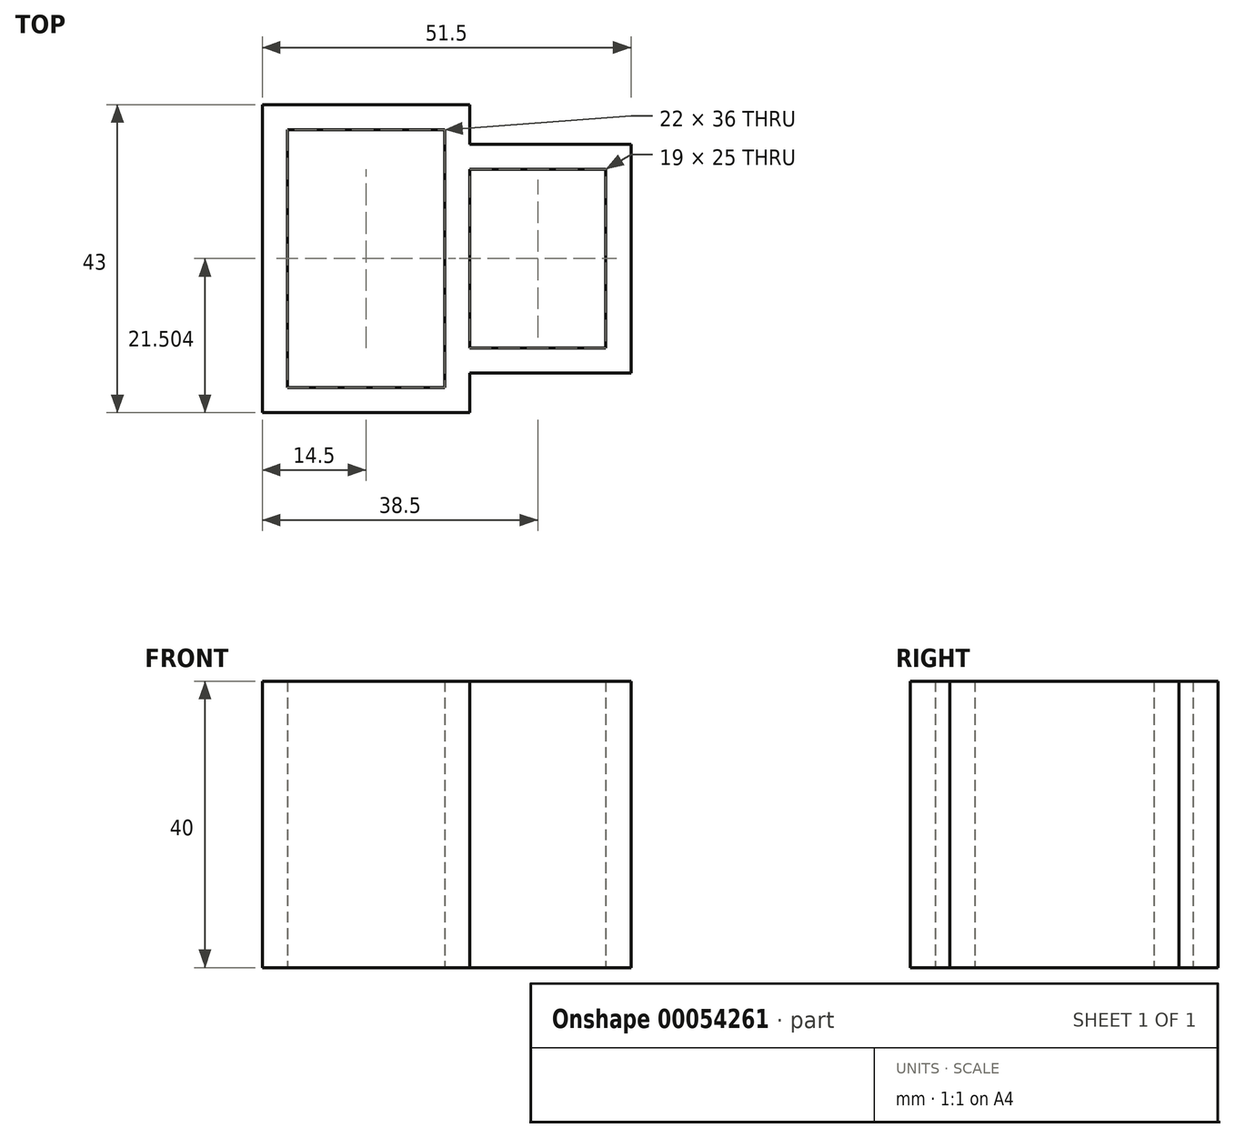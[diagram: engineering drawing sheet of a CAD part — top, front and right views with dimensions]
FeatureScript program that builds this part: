
annotation { "Feature Type Name" : "Feature", "Feature Type Description" : "" }
export const myFeature = defineFeature(function(context is Context, id is Id, definition is map)
    precondition{}
    {
        {
            var Q0;
            Q0=qCreatedBy(makeId("Top.planeOp"),FACE);
            var sketch = newSketch(context, id + "F0", { "sketchPlane" : qUnion([Q0])});
            skLineSegment(sketch, "E0.bottom", {"start": v(0, -10.9) * mm, "end": v(19, -10.9) * mm});
            skLineSegment(sketch, "E0.top", {"start": v(0, 14.1) * mm, "end": v(19, 14.1) * mm});
            skLineSegment(sketch, "E0.left", {"start": v(0, -10.9) * mm, "end": v(0, 14.1) * mm});
            skLineSegment(sketch, "E0.right", {"start": v(19, -10.9) * mm, "end": v(19, 14.1) * mm});
            skLineSegment(sketch, "E1.0", {"start": v(0, 17.6) * mm, "end": v(22.5, 17.6) * mm});
            skLineSegment(sketch, "E1.1", {"start": v(-3.5, -14.4) * mm, "end": v(-3.5, 17.6) * mm});
            skLineSegment(sketch, "E1.2", {"start": v(0, -14.4) * mm, "end": v(22.5, -14.4) * mm});
            skLineSegment(sketch, "E1.3", {"start": v(22.5, -14.4) * mm, "end": v(22.5, 17.6) * mm});
            skLineSegment(sketch, "E2.0", {"start": v(-25.5, -8.02) * mm, "end": v(-25.5, 11.23) * mm});
            skPoint(sketch, "E3", {"position": v(-25.5, 1.6) * mm});
            skLineSegment(sketch, "E4.0", {"start": v(-29, -8.02) * mm, "end": v(-29, 23.98) * mm});
            skLineSegment(sketch, "E5", {"start": v(-25.5, 1.6) * mm, "end": v(22.5, 1.6) * mm, "construction": true});
            skLineSegment(sketch, "E6.0", {"start": v(-25.5, -16.4) * mm, "end": v(-3.5, -16.4) * mm});
            skLineSegment(sketch, "E7.MirrorCS", {"start": v(-25.5, 19.6) * mm, "end": v(-3.5, 19.6) * mm});
            skLineSegment(sketch, "E8", {"start": v(-3.5, 17.6) * mm, "end": v(-3.5, 19.6) * mm});
            skLineSegment(sketch, "E9", {"start": v(-3.5, 19.6) * mm, "end": v(-3.5, -14.4) * mm});
            skLineSegment(sketch, "E10", {"start": v(-3.5, -14.4) * mm, "end": v(-3.5, -16.4) * mm});
            skLineSegment(sketch, "E11", {"start": v(-25.5, 19.6) * mm, "end": v(-25.5, 11.23) * mm});
            skLineSegment(sketch, "E12", {"start": v(-25.5, -8.02) * mm, "end": v(-25.5, -16.4) * mm});
            skPoint(sketch, "E13.orphan", {"position": v(22.5, 19.6) * mm});
            skPoint(sketch, "E14.orphan", {"position": v(22.5, -16.4) * mm});
            skLineSegment(sketch, "E15", {"start": v(-29, 23.98) * mm, "end": v(-29, 19.6) * mm});
            skLineSegment(sketch, "E16", {"start": v(-29, -8.02) * mm, "end": v(-29, -16.4) * mm});
            skLineSegment(sketch, "E17.0", {"start": v(-25.5, 23.1) * mm, "end": v(-29, 23.1) * mm});
            skLineSegment(sketch, "E17.1", {"start": v(-25.5, 23.1) * mm, "end": v(-3.5, 23.1) * mm});
            skLineSegment(sketch, "E18.MirrorCS", {"start": v(-25.5, -19.9) * mm, "end": v(-3.5, -19.9) * mm});
            skLineSegment(sketch, "E19", {"start": v(-29, -16.4) * mm, "end": v(-29, -19.9) * mm});
            skLineSegment(sketch, "E20", {"start": v(-29, -19.9) * mm, "end": v(-25.5, -19.9) * mm});
            skLineSegment(sketch, "E21.0", {"start": v(0, -10.88) * mm, "end": v(0, -10.9) * mm});
            skLineSegment(sketch, "E21.1", {"start": v(0, -8.77) * mm, "end": v(0, -10.88) * mm});
            skLineSegment(sketch, "E21.2", {"start": v(0, 22.42) * mm, "end": v(0, 17.6) * mm});
            skLineSegment(sketch, "E21.3", {"start": v(0, 23.1) * mm, "end": v(0, 22.42) * mm});
            skLineSegment(sketch, "E22", {"start": v(-3.5, 23.1) * mm, "end": v(0, 23.1) * mm});
            skLineSegment(sketch, "E23", {"start": v(-3.5, -19.9) * mm, "end": v(0, -19.9) * mm});
            skLineSegment(sketch, "E24.trimOffspring", {"start": v(0, 14.1) * mm, "end": v(0, -8.77) * mm});
            skLineSegment(sketch, "E25.trimOffspring", {"start": v(0, -14.4) * mm, "end": v(0, -19.9) * mm});
            skSolve(sketch);
        }
        {
            var Q0;
            Q0=makeQuery(id+"F0.imprint","IMPRINT",FACE,{"disambiguationData":[TD([[makeQuery(id+"F0.imprint","IMPRINT",EDGE,{"derivedFrom":sQuery(id+"F0.wireOp",EDGE,"E0.bottom")}),-1.0]])]});
            extrude(context, id + "F1", {"entities" : qUnion([Q0]), "depth" : 40 * mm});
        }
    });
